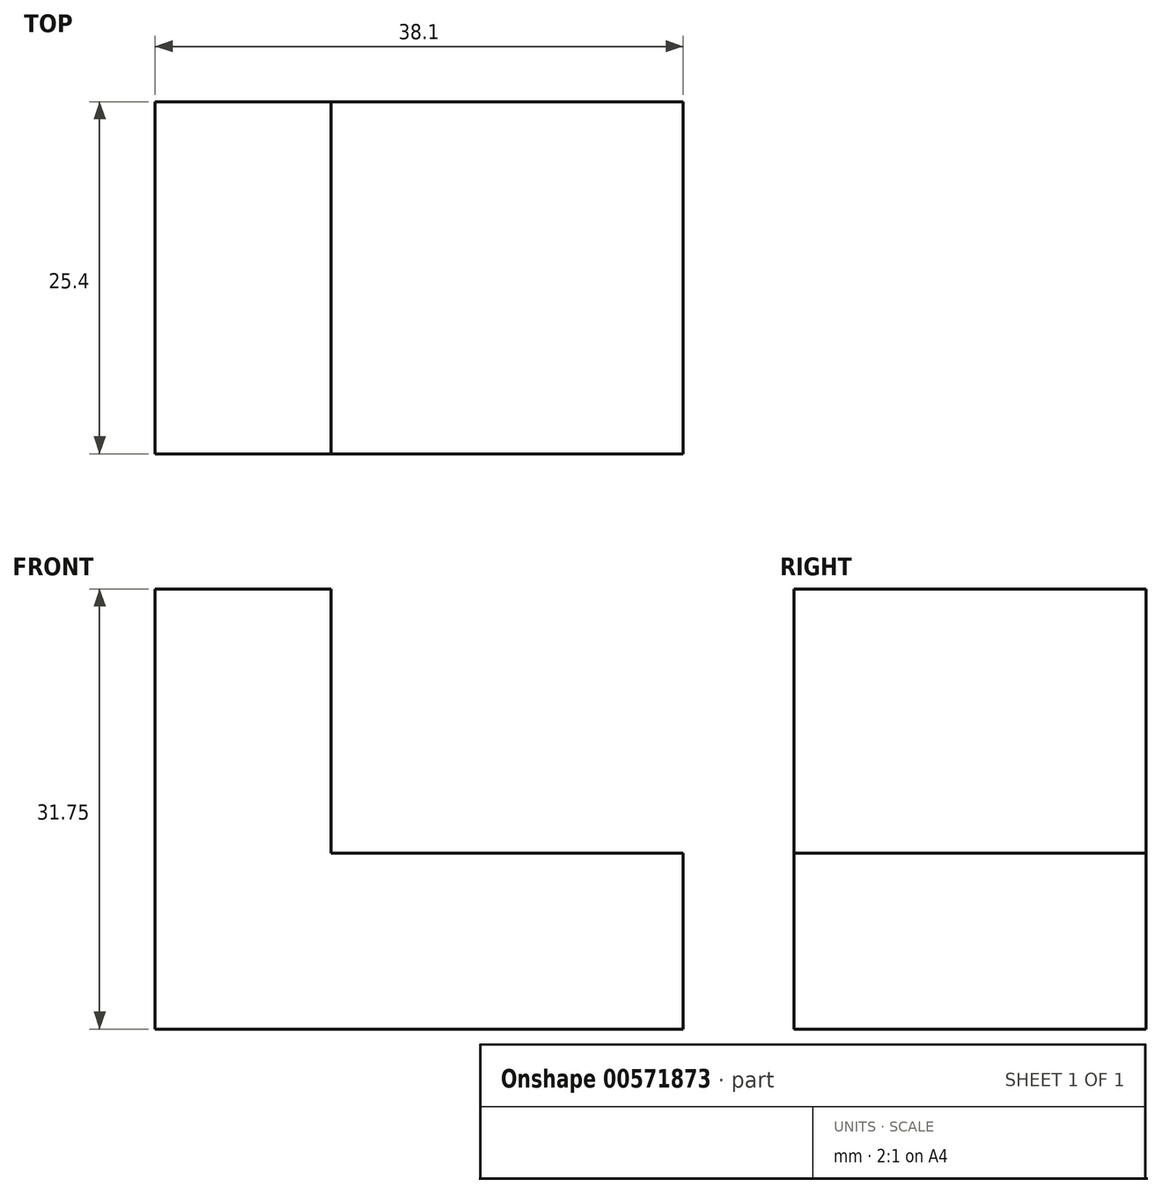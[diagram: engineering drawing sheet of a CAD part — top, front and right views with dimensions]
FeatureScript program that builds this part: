
annotation { "Feature Type Name" : "Feature", "Feature Type Description" : "" }
export const myFeature = defineFeature(function(context is Context, id is Id, definition is map)
    precondition{}
    {
        {
            var Q0;
            Q0=qCreatedBy(makeId("Front.planeOp"),FACE);
            var sketch = newSketch(context, id + "F0", { "sketchPlane" : qUnion([Q0])});
            skLineSegment(sketch, "E0", {"start": v(3.01, 31.75) * mm, "end": v(3.01, 0) * mm});
            skLineSegment(sketch, "E1", {"start": v(3.01, 0) * mm, "end": v(41.11, 0) * mm});
            skLineSegment(sketch, "E2", {"start": v(41.11, 0) * mm, "end": v(41.11, 12.7) * mm});
            skLineSegment(sketch, "E3", {"start": v(41.11, 12.7) * mm, "end": v(15.71, 12.7) * mm});
            skLineSegment(sketch, "E4", {"start": v(15.71, 12.7) * mm, "end": v(15.71, 31.75) * mm});
            skLineSegment(sketch, "E5", {"start": v(15.71, 31.75) * mm, "end": v(3.01, 31.75) * mm});
            skSolve(sketch);
        }
        {
            var Q0;
            Q0=makeQuery(id+"F0.imprint","IMPRINT",FACE,{"disambiguationData":[TD([[makeQuery(id+"F0.imprint","IMPRINT",EDGE,{"derivedFrom":sQuery(id+"F0.wireOp",EDGE,"E0")}),1.0]])]});
            extrude(context, id + "F1", {"entities" : qUnion([Q0]), "depth" : 25.4 * mm, "offsetDistance" : 25.4 * mm});
        }
    });
